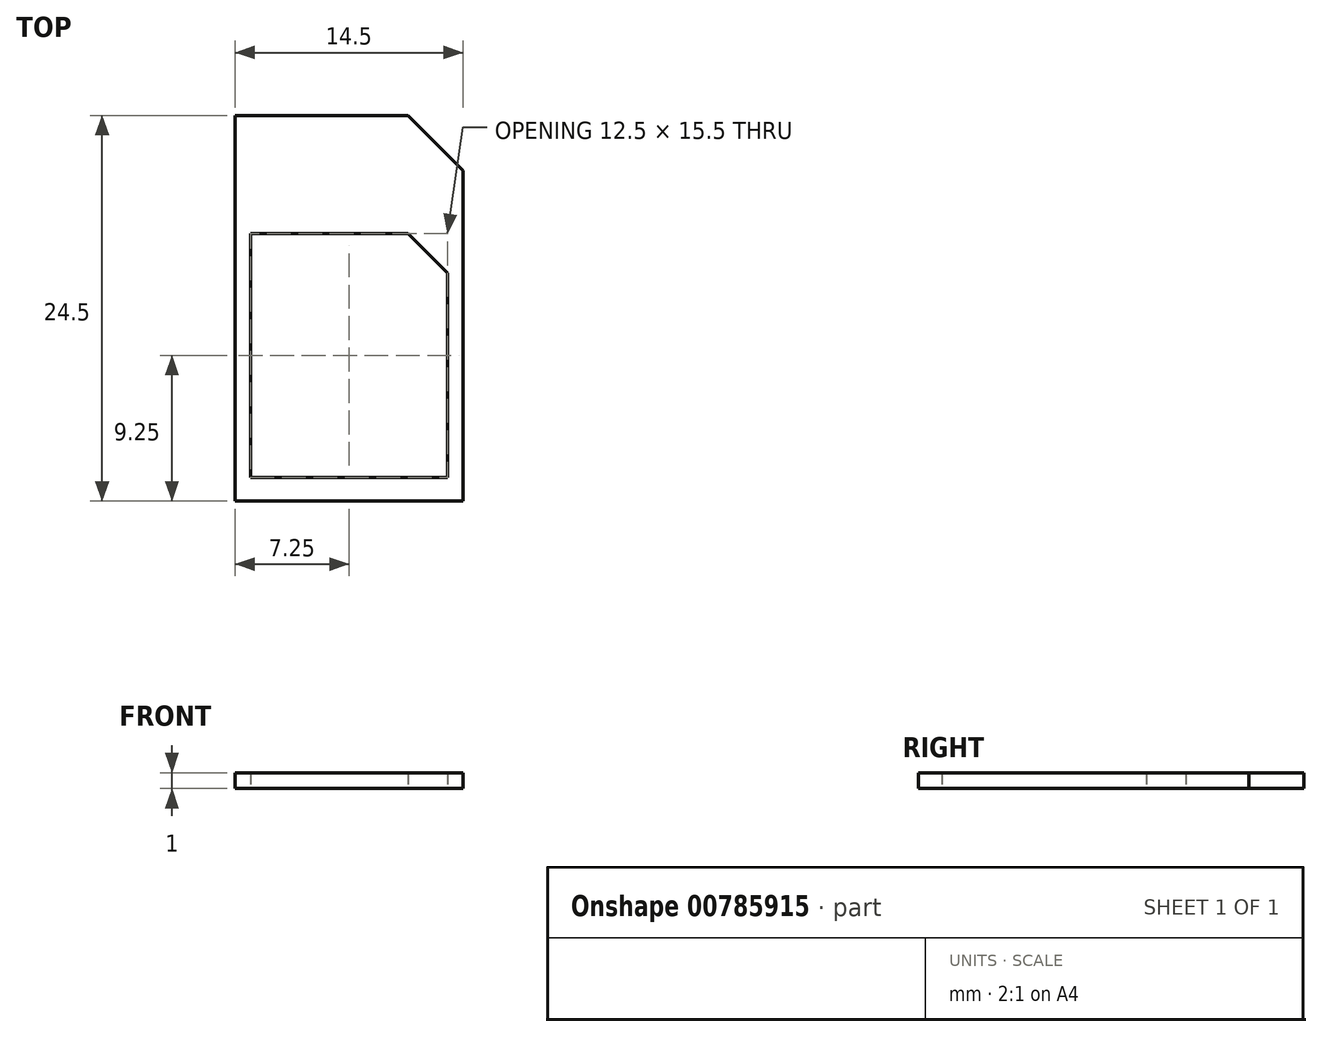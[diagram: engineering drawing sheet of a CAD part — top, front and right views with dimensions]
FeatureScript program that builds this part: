
annotation { "Feature Type Name" : "Feature", "Feature Type Description" : "" }
export const myFeature = defineFeature(function(context is Context, id is Id, definition is map)
    precondition{}
    {
        {
            var Q0;
            Q0=qCreatedBy(makeId("Top.planeOp"),FACE);
            var sketch = newSketch(context, id + "F0", { "sketchPlane" : qUnion([Q0])});
            skLineSegment(sketch, "E0.bottom", {"start": v(7.25, -12.25) * mm, "end": v(-7.25, -12.25) * mm});
            skLineSegment(sketch, "E0.top", {"start": v(3.75, 12.25) * mm, "end": v(-7.25, 12.25) * mm});
            skLineSegment(sketch, "E0.left", {"start": v(7.25, -12.25) * mm, "end": v(7.25, 8.75) * mm});
            skLineSegment(sketch, "E0.right", {"start": v(-7.25, -12.25) * mm, "end": v(-7.25, 12.25) * mm});
            skPoint(sketch, "E0.middle", {"position": v(0, 0) * mm});
            skLineSegment(sketch, "E1", {"start": v(7.25, 8.75) * mm, "end": v(3.75, 12.25) * mm});
            skPoint(sketch, "E2.orphan", {"position": v(7.25, 12.25) * mm});
            skLineSegment(sketch, "E3.bottom", {"start": v(6.25, -10.75) * mm, "end": v(-6.25, -10.75) * mm});
            skLineSegment(sketch, "E3.top", {"start": v(3.75, 4.75) * mm, "end": v(-6.25, 4.75) * mm});
            skLineSegment(sketch, "E3.left", {"start": v(6.25, -10.75) * mm, "end": v(6.25, 2.25) * mm});
            skLineSegment(sketch, "E3.right", {"start": v(-6.25, -10.75) * mm, "end": v(-6.25, 4.75) * mm});
            skPoint(sketch, "E3.middle", {"position": v(0, -3) * mm});
            skLineSegment(sketch, "E4", {"start": v(6.25, 2.25) * mm, "end": v(3.75, 4.75) * mm});
            skPoint(sketch, "E5.orphan", {"position": v(6.25, 4.75) * mm});
            skSolve(sketch);
        }
        {
            var Q0;
            Q0 = qSketchRegion(id + "F0", true);
            var Q1;
            {var subQ3=sQuery(id+"F0.wireOp",EDGE,"E4");Q1=makeQuery(id+"F0.imprint","IMPRINT",FACE,{"disambiguationData":[TD([[makeQuery(id+"F0.imprint","IMPRINT",EDGE,{"derivedFrom":subQ3}),-1.0]])]});}
            extrude(context, id + "F1", {"entities" : qUnion([Q0, Q1]), "depth" : 1 * mm, "offsetDistance" : 25 * mm});
        }
    });
